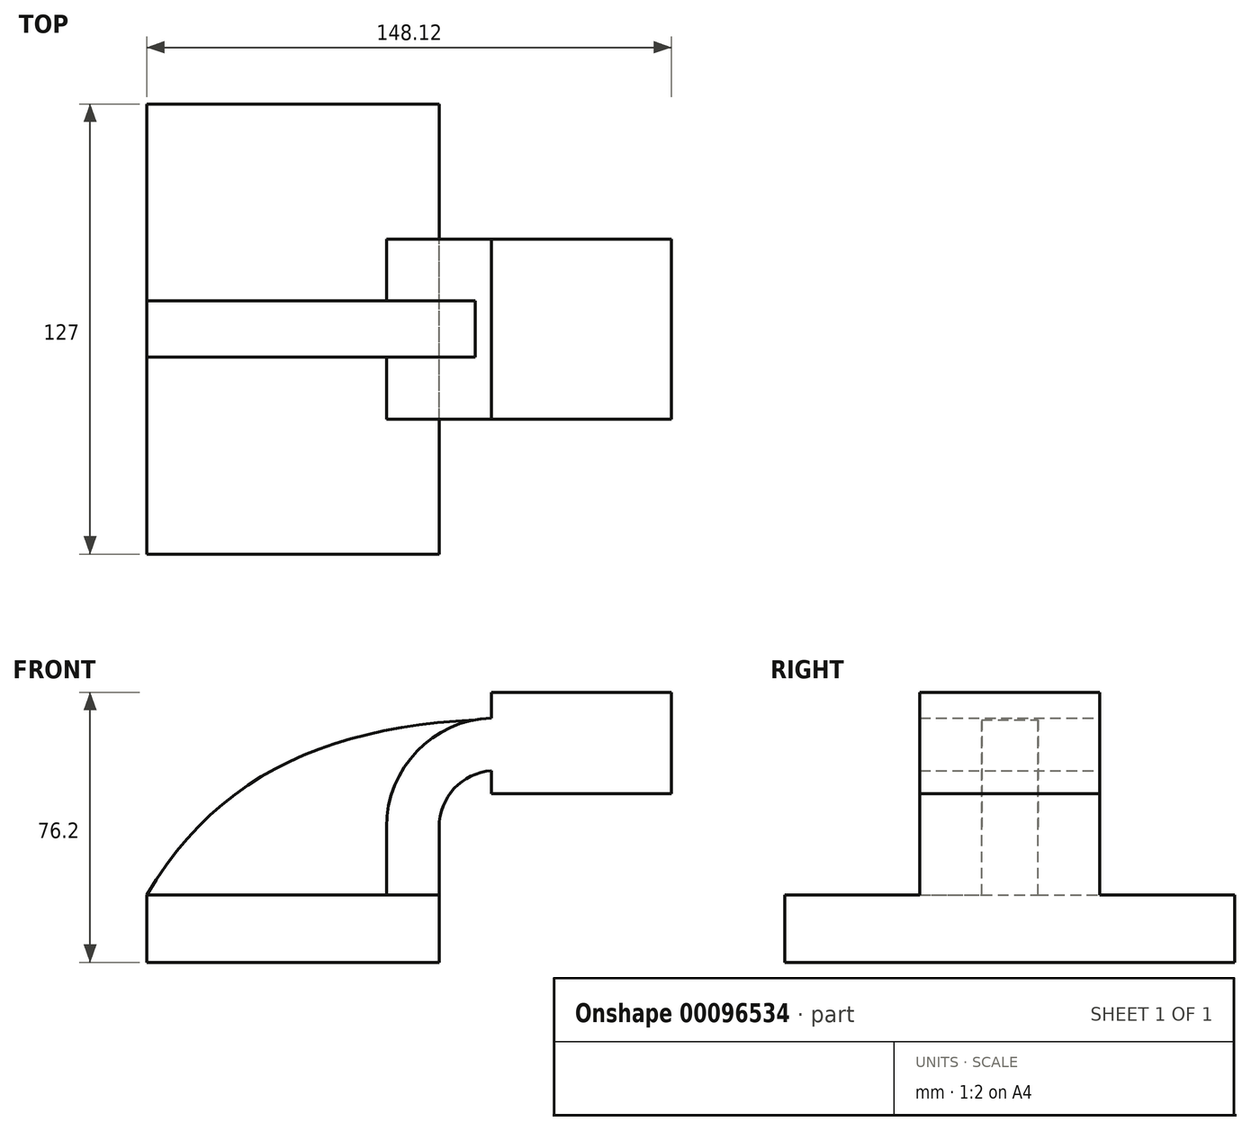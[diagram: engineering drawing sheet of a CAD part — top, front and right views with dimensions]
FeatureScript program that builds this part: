
annotation { "Feature Type Name" : "Feature", "Feature Type Description" : "" }
export const myFeature = defineFeature(function(context is Context, id is Id, definition is map)
    precondition{}
    {
        {
            var Q0;
            Q0=qCreatedBy(makeId("Front.planeOp"),FACE);
            var sketch = newSketch(context, id + "F0", { "sketchPlane" : qUnion([Q0])});
            skLineSegment(sketch, "E0.bottom", {"start": v(-41.28, 9.52) * mm, "end": v(41.28, 9.53) * mm});
            skLineSegment(sketch, "E0.top", {"start": v(-41.28, -9.53) * mm, "end": v(41.28, -9.53) * mm});
            skLineSegment(sketch, "E0.left", {"start": v(-41.28, 9.52) * mm, "end": v(-41.28, -9.53) * mm});
            skLineSegment(sketch, "E0.right", {"start": v(41.28, 9.53) * mm, "end": v(41.28, -9.52) * mm});
            skPoint(sketch, "E0.middle", {"position": v(0, 0) * mm});
            skLineSegment(sketch, "E1.bottom", {"start": v(56.04, 38.1) * mm, "end": v(106.84, 38.1) * mm});
            skLineSegment(sketch, "E1.top", {"start": v(56.04, 66.67) * mm, "end": v(106.84, 66.67) * mm});
            skLineSegment(sketch, "E1.left", {"start": v(56.04, 38.1) * mm, "end": v(56.04, 66.67) * mm});
            skLineSegment(sketch, "E1.right", {"start": v(106.84, 38.1) * mm, "end": v(106.84, 66.67) * mm});
            skPoint(sketch, "E1.middle", {"position": v(81.44, 52.39) * mm});
            skLineSegment(sketch, "E2", {"start": v(41.27, 9.53) * mm, "end": v(41.27, 28.68) * mm});
            skArc(sketch, "E3", {"start": v(41.27, 28.68) * mm, "mid": v(45.92, 39.9) * mm, "end": v(57.15, 44.56) * mm});
            skLineSegment(sketch, "E4", {"start": v(57.15, 44.56) * mm, "end": v(83.1, 44.56) * mm});
            skArc(sketch, "E5.0", {"start": v(47.62, 28.68) * mm, "mid": v(50.41, 35.42) * mm, "end": v(57.15, 38.2) * mm});
            skLineSegment(sketch, "E6.0", {"start": v(57.15, 59.46) * mm, "end": v(83.1, 59.46) * mm});
            skArc(sketch, "E6.1", {"start": v(26.38, 28.68) * mm, "mid": v(35.39, 50.44) * mm, "end": v(57.15, 59.46) * mm});
            skLineSegment(sketch, "E6.2", {"start": v(26.38, 9.53) * mm, "end": v(26.38, 28.68) * mm});
            skFitSpline(sketch, "E7", {"points": [v(-41.28, 9.52) * mm, v(51.4, 58.92) * mm], "startDerivative": vector(60.58, 101.84) * mm, "endDerivative": vector(125.68, 7) * mm});
            skSolve(sketch);
        }
        {
            var Q0;
            Q0=makeQuery(id+"F0.imprint","IMPRINT",FACE,{"disambiguationData":[TD([[makeQuery(id+"F0.imprint","IMPRINT",EDGE,{"derivedFrom":sQuery(id+"F0.wireOp",EDGE,"E0.top")}),1.0]])]});
            extrude(context, id + "F1", {"entities" : qUnion([Q0]), "endBound" : BoundingType.SYMMETRIC, "depth" : 127 * mm});
        }
        {
            var Q0;
            {var subQ1=sQuery(id+"F0.wireOp",EDGE,"E2");Q0=makeQuery(id+"F0.imprint","IMPRINT",FACE,{"disambiguationData":[TD([[makeQuery(id+"F0.imprint","IMPRINT",EDGE,{"derivedFrom":subQ1}),1.0]])]});}
            var Q1;
            {var subQ3=sQuery(id+"F0.wireOp",EDGE,"E1.bottom");Q1=makeQuery(id+"F0.imprint","IMPRINT",FACE,{"disambiguationData":[TD([[makeQuery(id+"F0.imprint","IMPRINT",EDGE,{"derivedFrom":subQ3}),1.0]])]});}
            extrude(context, id + "F2", {"entities" : qUnion([Q0, Q1]), "operationType" : NewBodyOperationType.ADD, "endBound" : BoundingType.SYMMETRIC, "depth" : 50.8 * mm});
        }
        {
            var Q0;
            {var subQ2=sQuery(id+"F0.wireOp",EDGE,"E6.2");Q0=makeQuery(id+"F0.imprint","IMPRINT",FACE,{"disambiguationData":[TD([[makeQuery(id+"F0.imprint","IMPRINT",EDGE,{"derivedFrom":subQ2}),1.0]])]});}
            extrude(context, id + "F3", {"entities" : qUnion([Q0]), "operationType" : NewBodyOperationType.ADD, "endBound" : BoundingType.SYMMETRIC, "depth" : 15.88 * mm});
        }
    });
